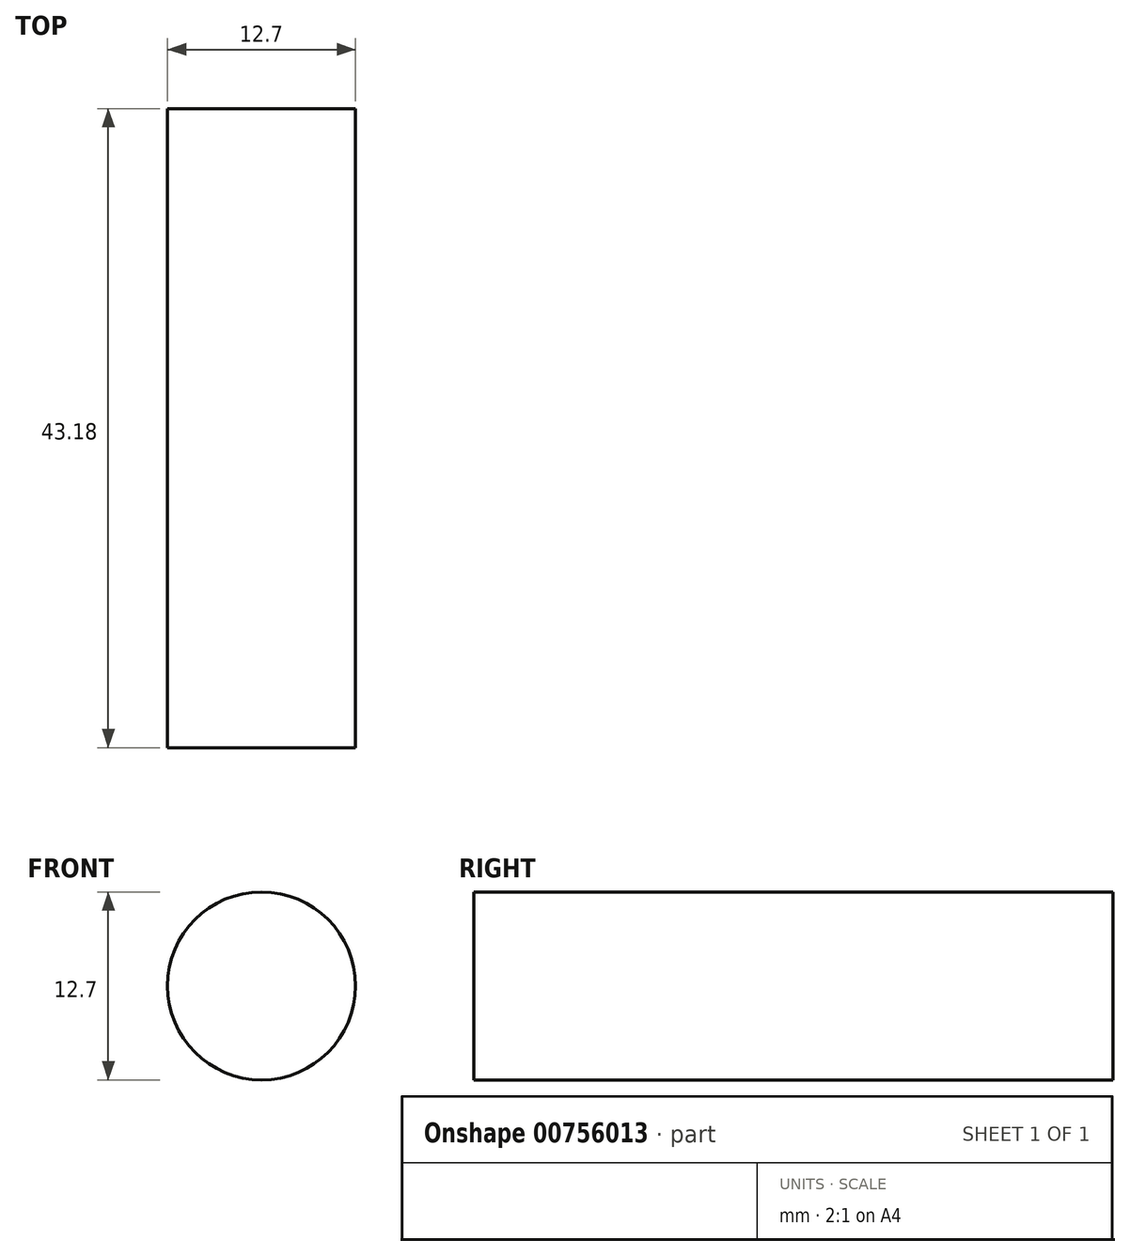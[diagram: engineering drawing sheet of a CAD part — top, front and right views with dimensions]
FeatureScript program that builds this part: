
annotation { "Feature Type Name" : "Feature", "Feature Type Description" : "" }
export const myFeature = defineFeature(function(context is Context, id is Id, definition is map)
    precondition{}
    {
        {
            var Q0;
            Q0=qCreatedBy(makeId("Front.planeOp"),FACE);
            var sketch = newSketch(context, id + "F0", { "sketchPlane" : qUnion([Q0])});
            skCircle(sketch, "E0", {"center": v(0, 0) * mm, "radius": 6.35 * mm});
            skSolve(sketch);
        }
        {
            var Q0;
            Q0=makeQuery(id+"F0.imprint","IMPRINT",FACE,{"disambiguationData":[TD([[makeQuery(id+"F0.imprint","IMPRINT",EDGE,{"derivedFrom":sQuery(id+"F0.wireOp",EDGE,"E0")}),1.0]])]});
            extrude(context, id + "F1", {"entities" : qUnion([Q0]), "depth" : 43.18 * mm, "offsetDistance" : 25.4 * mm});
        }
    });
